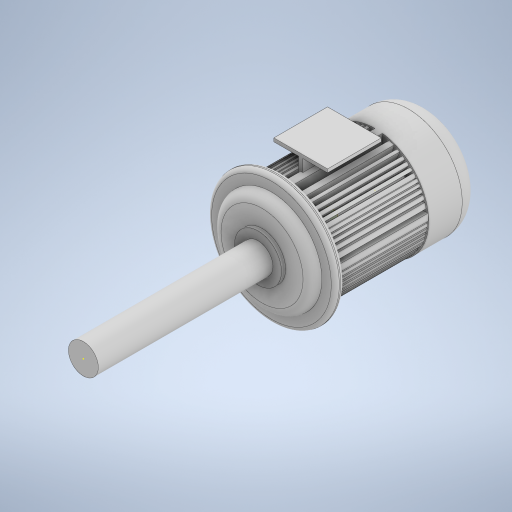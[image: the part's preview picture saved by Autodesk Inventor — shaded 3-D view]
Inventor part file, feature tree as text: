
AUTODESK INVENTOR PART (.ipt)
format: ipt  version: 2023 (Build 270158000, 158)  size: 854,016 bytes
history: native  units: in
note: dims shown in document units (in); Inventor stores cm internally (conversion verified against a paired STEP export)
features: sketch x71, extrude x68, fillet x4, plane x1
ambient origin geometry x8: Origin, YZ Plane, XZ Plane, XY Plane, X Axis, Y Axis, Z Axis, Center Point
bodies: Solid1 (feature_tree)
feature tree (144):
  extrude  "Extrusion1"  Depth=1.5748in TaperAngle=0.0deg
  sketch  "Sketch2"  dims[d3=2.3622in d4=0.0172in]
  extrude  "Extrusion2"  Depth=0.0172in
  extrude  "Extrusion3"  Depth=2.7559in
  extrude  "Extrusion4"  Depth=2.7559in
  extrude  "Extrusion5"  Depth=2.7559in
  sketch  "Sketch7"  dims[d17=2.7559in d18=0.0in d19=2.7559in d20=0.0in]
  extrude  "Extrusion6"  Depth=2.7559in TaperAngle=0.0deg
  extrude  "Extrusion7"  Depth=2.7559in TaperAngle=0.0deg
  extrude  "Extrusion8"  Depth=2.7559in TaperAngle=0.0deg
  extrude  "Extrusion9"  Depth=2.7559in TaperAngle=0.0deg
  extrude  "Extrusion10"  Depth=2.7559in TaperAngle=0.0deg
  extrude  "Extrusion11"  Depth=2.7559in TaperAngle=0.0deg
  extrude  "Extrusion12"  Depth=2.7559in TaperAngle=0.0deg
  extrude  "Extrusion13"  Depth=2.7559in TaperAngle=0.0deg
  extrude  "Extrusion14"  Depth=2.7559in TaperAngle=0.0deg
  extrude  "Extrusion15"  Depth=2.7559in TaperAngle=0.0deg
  extrude  "Extrusion16"  Depth=2.7559in TaperAngle=0.0deg
  extrude  "Extrusion17"  Depth=2.7559in TaperAngle=0.0deg
  extrude  "Extrusion18"  Depth=2.7559in TaperAngle=0.0deg
  extrude  "Extrusion19"  Depth=2.7559in TaperAngle=0.0deg
  extrude  "Extrusion20"  Depth=2.7559in TaperAngle=0.0deg
  extrude  "Extrusion21"  Depth=2.7559in TaperAngle=0.0deg
  extrude  "Extrusion22"  Depth=2.7559in TaperAngle=0.0deg
  extrude  "Extrusion23"  Depth=2.7559in TaperAngle=0.0deg
  extrude  "Extrusion24"  Depth=2.7559in TaperAngle=0.0deg
  extrude  "Extrusion25"  Depth=2.7559in TaperAngle=0.0deg
  extrude  "Extrusion26"  Depth=2.7559in TaperAngle=0.0deg
  extrude  "Extrusion27"  Depth=2.7559in TaperAngle=0.0deg
  extrude  "Extrusion28"  Depth=2.7559in TaperAngle=0.0deg
  extrude  "Extrusion29"  Depth=2.7559in TaperAngle=0.0deg
  extrude  "Extrusion30"  Depth=2.7559in TaperAngle=0.0deg
  extrude  "Extrusion31"  Depth=2.7559in TaperAngle=0.0deg
  extrude  "Extrusion32"  Depth=2.7559in TaperAngle=0.0deg
  extrude  "Extrusion33"  Depth=2.7559in TaperAngle=0.0deg
  extrude  "Extrusion34"  Depth=0.2756in TaperAngle=0.0deg
  extrude  "Extrusion35"  Depth=0.2756in TaperAngle=0.0deg
  extrude  "Extrusion36"  Depth=0.1181in
  extrude  "Extrusion37"  Depth=0.1181in
  extrude  "Extrusion38"  Depth=0.1181in
  extrude  "Extrusion39"  Depth=0.5906in
  extrude  "Extrusion40"  Depth=0.7874in TaperAngle=0.0deg
  extrude  "Extrusion41"  Depth=1.5748in TaperAngle=0.0deg
  extrude  "Extrusion42"  Depth=2.8312in TaperAngle=0.0deg
  extrude  "Extrusion43"  Depth=1.9291in
  extrude  "Extrusion44"  TaperAngle=180.0deg  [1 undecoded]
  extrude  "Extrusion45"  Depth=1.5748in TaperAngle=0.0deg
  extrude  "Extrusion46"  [1 undecoded]
  extrude  "Extrusion47"  [1 undecoded]
  extrude  "Extrusion48"  [1 undecoded]
  extrude  "Extrusion49"  [1 undecoded]
  extrude  "Extrusion50"  [1 undecoded]
  extrude  "Extrusion51"  [1 undecoded]
  extrude  "Extrusion52"  [1 undecoded]
  extrude  "Extrusion53"  [1 undecoded]
  extrude  "Extrusion54"  [1 undecoded]
  extrude  "Extrusion55"  [1 undecoded]
  extrude  "Extrusion56"  [1 undecoded]
  extrude  "Extrusion57"  [1 undecoded]
  extrude  "Extrusion58"  [1 undecoded]
  extrude  "Extrusion59"  [1 undecoded]
  extrude  "Extrusion60"  [1 undecoded]
  extrude  "Extrusion61"  [1 undecoded]
  fillet  "Fillet1"  [1 undecoded]
  fillet  "Fillet2"  [1 undecoded]
  fillet  "Fillet3"  [1 undecoded]
  extrude  "Extrusion62"  [1 undecoded]
  extrude  "Extrusion63"  [1 undecoded]
  fillet  "Fillet4"  [1 undecoded]
  extrude  "Extrusion64"  [1 undecoded]
  extrude  "Extrusion65"  [1 undecoded]
  sketch  "Sketch67"
  sketch  "Sketch68"
  extrude  "Extrusion66"  [1 undecoded]
  extrude  "Extrusion67"  [1 undecoded]
  plane  "Work Plane1"
  extrude  "Extrusion68"  [1 undecoded]
  sketch  "Sketch1"  dims[d0=3.1496in d1=1.5748in d2=0.0in]
  sketch  "Sketch3"  dims[d5=2.7559in d6=0.0in d7=0.0984in]
  sketch  "Sketch4"  dims[d8=2.7559in d9=0.0in d10=0.0984in]
  sketch  "Sketch5"  dims[d11=2.7559in d12=0.0in d13=0.0984in]
  sketch  "Sketch6"  dims[d14=0.0984in d15=2.7559in d16=0.0in]
  sketch  "Sketch8"  dims[d21=2.7559in d22=0.0in d23=2.7559in d24=0.0in]
  sketch  "Sketch9"  dims[d25=2.7559in d26=0.0in d27=2.7559in d28=0.0in]
  sketch  "Sketch10"  dims[d29=2.7559in d30=0.0in d31=2.7559in d32=0.0in]
  sketch  "Sketch11"  dims[d33=2.7559in d34=0.0in d35=2.7559in d36=0.0in]
  sketch  "Sketch12"  dims[d37=2.7559in d38=0.0in d39=2.7559in d40=0.0in]
  sketch  "Sketch13"  dims[d41=2.7559in d42=0.0in d43=2.7559in d44=0.0in]
  sketch  "Sketch14"  dims[d45=2.7559in d46=0.0in d47=2.7559in d48=0.0in]
  sketch  "Sketch15"  dims[d49=2.7559in d50=0.0in d51=2.7559in d52=0.0in]
  sketch  "Sketch16"  dims[d53=2.7559in d54=0.0in d55=2.7559in d56=0.0in]
  sketch  "Sketch17"  dims[d57=2.7559in d58=0.0in d59=2.7559in d60=0.0in]
  sketch  "Sketch18"  dims[d61=2.7559in d62=0.0in d63=2.7559in d64=0.0in]
  sketch  "Sketch19"  dims[d65=2.7559in d66=0.0in d67=2.7559in d68=0.0in]
  sketch  "Sketch20"  dims[d69=2.7559in d70=0.0in d71=2.7559in d72=0.0in]
  sketch  "Sketch21"  dims[d73=2.7559in d74=0.0in d75=2.7559in d76=0.0in]
  sketch  "Sketch22"  dims[d77=2.7559in d78=0.0in d79=2.7559in d80=0.0in]
  sketch  "Sketch23"  dims[d81=2.7559in d82=0.0in d83=2.7559in d84=0.0in]
  sketch  "Sketch24"  dims[d85=2.7559in d86=0.0in d87=2.7559in d88=0.0in]
  sketch  "Sketch25"  dims[d89=2.7559in d90=0.0in d91=2.7559in d92=0.0in]
  sketch  "Sketch26"  dims[d93=2.7559in d94=0.0in d95=2.7559in d96=0.0in]
  sketch  "Sketch27"  dims[d97=2.7559in d98=0.0in d99=2.7559in d100=0.0in]
  sketch  "Sketch28"  dims[d101=2.7559in d102=0.0in d103=2.7559in d104=0.0in]
  sketch  "Sketch29"  dims[d105=2.7559in d106=0.0in d107=2.7559in d108=0.0in]
  sketch  "Sketch30"  dims[d109=2.7559in d110=0.0in d111=2.7559in d112=0.0in]
  sketch  "Sketch31"  dims[d113=2.7559in d114=0.0in d115=2.7559in d116=0.0in]
  sketch  "Sketch32"  dims[d117=2.7559in d118=0.0in d119=2.7559in d120=0.0in]
  sketch  "Sketch33"  dims[d121=2.7559in d122=0.0in d123=2.7559in d124=0.0in]
  sketch  "Sketch34"  dims[d125=3.7402in d126=0.2756in d127=0.0in]
  sketch  "Sketch35"  dims[d128=2.9528in d129=0.2756in d130=0.0in]
  sketch  "Sketch36"  dims[d131=0.2756in d132=0.1181in]
  sketch  "Sketch37"  dims[d133=0.1181in d134=1.378in]
  sketch  "Sketch38"  dims[d135=0.1181in d136=0.0in d137=0.875in]
  sketch  "Sketch39"  dims[d138=5.1181in d139=0.0in d140=0.5906in]
  sketch  "Sketch40"  dims[d141=0.2088in d142=0.7874in d143=0.0in]
  sketch  "Sketch41"  dims[d144=0.2756in d145=1.5748in d146=0.0in]
  sketch  "Sketch42"  dims[d147=2.8312in d148=0.0in d149=2.8312in d150=0.0in]
  sketch  "Sketch43"  dims[d151=-3.75in d152=1.9291in]
  sketch  "Sketch44"  dims[d153=0.0991in d154=180.0deg]
  sketch  "Sketch45"  dims[d155=0.7874in d156=1.5748in d157=0.0in]
  sketch  "Sketch46"
  sketch  "Sketch47"
  sketch  "Sketch48"
  sketch  "Sketch49"
  sketch  "Sketch50"
  sketch  "Sketch51"
  sketch  "Sketch52"
  sketch  "Sketch53"
  sketch  "Sketch54"
  sketch  "Sketch55"
  sketch  "Sketch56"
  sketch  "Sketch57"
  sketch  "Sketch58"
  sketch  "Sketch59"
  sketch  "Sketch60"
  sketch  "Sketch61"
  sketch  "Sketch62"
  sketch  "Sketch63"
  sketch  "Sketch64"
  sketch  "Sketch65"
  sketch  "Sketch66"
  sketch  "Sketch69"
  sketch  "Sketch70"
  sketch  "Sketch71"
note: 28 required parameter values undecoded (feature->parameter linkage not recoverable at this tier; creation-order binding heuristic only, values carry confidence <= 0.55)
